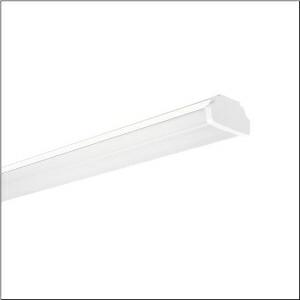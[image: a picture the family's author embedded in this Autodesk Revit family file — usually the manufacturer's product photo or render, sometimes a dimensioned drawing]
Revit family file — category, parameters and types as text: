
# Revit family: modario_r__31_mo_53bm812m1v4085_4dae
name_source: partatom
category: Lighting Fixtures
units: mm (PartAtom-declared; Revit-internal decimal feet)

## family parameters
Cut with Voids When Loaded = No
Host = Face
Light Source = No
Part Type = Normal
Room Calculation Point = No
Round Connector Dimension = Use Diameter
Shared = No

## types (1)
- --- (1 x LED, 8950 lm, 59.6 W, 4000K)
    Apparent Load = 60 VA
    CIE Flux Codes = 47 80 95 92 100
    Color Rendering = 80
    Color Temperature = 4000K
    Default Elevation = 1800 mm
    Description = Modario® 31 MOluminaire insert, length: 1.495mm, width: 81mm, height: 82mm, LED rated luminous flux: 8.950lm, light colour: 840, control gear: ON/OFF Multilumen, control gear: ECG Multilumen, with plug, 3-pole, with phase selection, mains connection: 220..240V, AC, 50/60Hz, primary optical cover: cover, of PMMA, light emission: direct distribution, primary light characteristic: symmetric, protection rating (complete): IP20, protection rating (LED compartment): IP50, insulation class (complete): insulation class I (protective earthing), certification: CE, ENEC, VDE, permissible ambient temperature for indoor applications: -35..+30°C, corresponds to IFS (International Featured Standards) requirements for safety and quality in the food industry, reducing of maximum allowable ambient temperature of 5°C with ceiling mounting, packaging unit: 1 piece
    Height = 92 mm
    Lamp = 1 x LED
    Lamp Light Flux = 8950 lm
    Lamp Power = 59.6 W
    Lamp count = 1
    Length = 1495 mm
    Luminous efficacy = 150 lm/W
    Manufacturer = Siteco
    ModVariant = No
    Model = 53BM812M1V4085
    Mounting Place = Ceiling
    Mounting Type = Pendant
    Number of Poles = 1
    OnlyDefault = Yes
    Power Factor = 1
    Product Name = Modario® 31 MO
    Product group = luminaire insert
    ProductGroupID = 902
    Protection Class = Protection class I
    Protection Degree = IP 20
    RLX_Detail_Level = 1
    RlxData = <blob elided: 39701 chars, md5=a60055a9>
    Socket = socket
    Standby Power = 0 W
    System Light Flux = 8950 lm
    System Power = 60 W
    Type Comments = factory setting: luminous flux: 100 % | (A | C | E) | 129 mA
    Type Image = l_1003447.jpg
    URL = http://relux.com
    VarID = @adj_133719
    Voltage = 0 V
    Weight = 0.00 kg
    Width = 81 mm

## geometry (parser evidence)
native form markers: Blend x4, Sweep x12
no freeform markers — native parametric forms only
